# Revit family: Power-ModularDevices-GEWISS-90AM-SWITCH_DISCONNECTOR_3P
name_source: partatom
category: Apparecchi elettrici
revit_build: Autodesk Revit 2016 (Build: 20161004_0715(x64)
units: mm (PartAtom-declared; Revit-internal decimal feet)

## family parameters
Condiviso = No
Host = Superficie
Mantenere orientamento annotazione = Sì
Numero OmniClass = 23.80.50.00
Punto di calcolo locali = Sì
Quota connettore circolare = Usa diametro
Taglio con vuoti quando caricato = No
Tipo di parte = Normale
Titolo OmniClass = Terminals for Power Supply

## types (6) — shared parameters
Catalogue = POWER
Catalogue Range = 90 AM
Electrocod = 1422
IDF = 39a902cc-11b3-4623-980f-404ddf05e9d1
IDT = 97457cef-319b-4fb2-b7b4-03318a77c985
Immagine tipo = GW96124.jpg
No. Chorus modules = 3
No. of modules EN 50022 = 3
No. of poles = 3P
Number of poles = 3P
Numero di poli = 1
Produttore = GEWISS S.p.A.
Prospetto di default = 1219 mm
Rated voltage = 415Vac
Rated voltage AC = 415V
SEO = Disconnector
Spostamento_x = -340 mm
Standard = EN 60947-3
Technical sheet = https://www.gewiss.com
URL = https://www.gewiss.com
Version file RFA = 18.0
carico = Altro
potenza in watt = 0 V

## per-type parameters (varying)
| type | Descrizione | EAN code | Modello | Rated current (In) | Rated current: |
| GW96169 - SWITCH DISCONNECTOR 3P 125A | SWITCH DISCONNECTOR 3P 125A | 8011564131729 | GW96169 | 125A | 125A |
| GW96124 - SWITCH DISCONNECTOR 3P 32A | SWITCH DISCONNECTOR 3P 32A | 8011564110373 | GW96124 | 32A | 32A |
| GW96167 - SWITCH DISCONNECTOR 3P 80A | SWITCH DISCONNECTOR 3P 80A | 8011564131705 | GW96167 | 80A | 80A |
| GW96166 - SWITCH DISCONNECTOR 3P 63A | SWITCH DISCONNECTOR 3P 63A | 8011564131699 | GW96166 | 63A | 63A |
| GW96125 - SWITCH DISCONNECTOR 3P 40A | SWITCH DISCONNECTOR 3P 40A | 8011564110380 | GW96125 | 40A | 40A |
| GW96168 - SWITCH DISCONNECTOR 3P 100A | SWITCH DISCONNECTOR 3P 100A | 8011564131712 | GW96168 | 100A | 100A |
